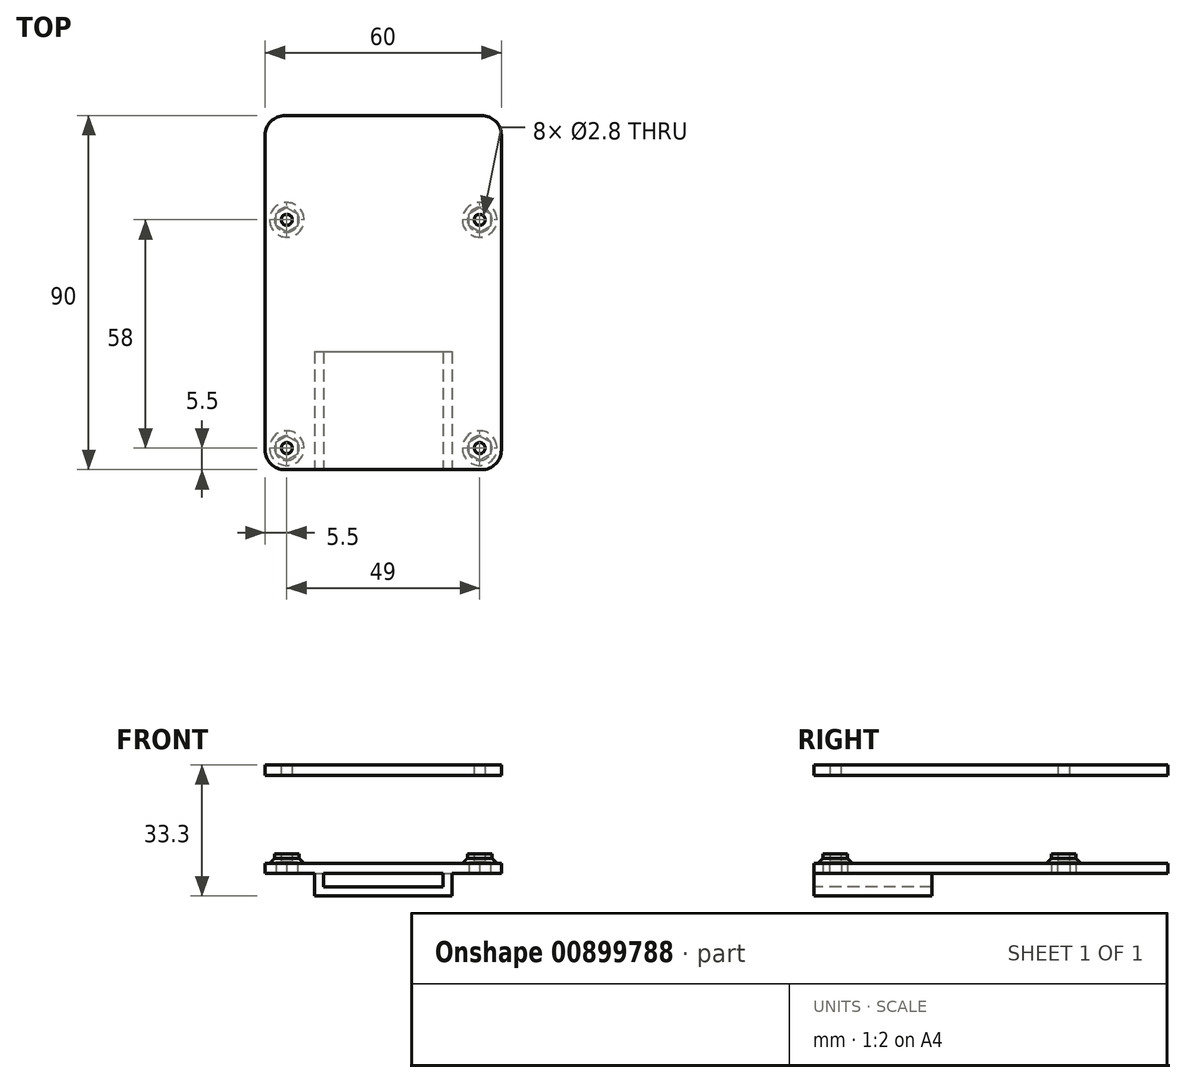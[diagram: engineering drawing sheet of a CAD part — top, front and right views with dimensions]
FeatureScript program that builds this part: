
annotation { "Feature Type Name" : "Feature", "Feature Type Description" : "" }
export const myFeature = defineFeature(function(context is Context, id is Id, definition is map)
    precondition{}
    {
        {
            var Q0;
            Q0=qCreatedBy(makeId("Top.planeOp"),FACE);
            var sketch = newSketch(context, id + "F0", { "sketchPlane" : qUnion([Q0])});
            skLineSegment(sketch, "E0.bottom", {"start": v(-30, 45) * mm, "end": v(30, 45) * mm});
            skLineSegment(sketch, "E0.top", {"start": v(-30, -45) * mm, "end": v(30, -45) * mm});
            skLineSegment(sketch, "E0.left", {"start": v(-30, 45) * mm, "end": v(-30, -45) * mm});
            skLineSegment(sketch, "E0.right", {"start": v(30, 45) * mm, "end": v(30, -45) * mm});
            skPoint(sketch, "E0.middle", {"position": v(0, 0) * mm});
            skLineSegment(sketch, "E1.bottom", {"start": v(-24.5, 18.5) * mm, "end": v(24.5, 18.5) * mm, "construction": true});
            skLineSegment(sketch, "E1.top", {"start": v(-24.5, -39.5) * mm, "end": v(24.5, -39.5) * mm, "construction": true});
            skLineSegment(sketch, "E1.left", {"start": v(-24.5, 18.5) * mm, "end": v(-24.5, -39.5) * mm, "construction": true});
            skLineSegment(sketch, "E1.right", {"start": v(24.5, 18.5) * mm, "end": v(24.5, -39.5) * mm, "construction": true});
            skPoint(sketch, "E1.middle", {"position": v(0, -10.5) * mm});
            skCircle(sketch, "E2", {"center": v(-24.5, 18.5) * mm, "radius": 1.4 * mm});
            skCircle(sketch, "E3", {"center": v(24.5, 18.5) * mm, "radius": 1.4 * mm});
            skCircle(sketch, "E4", {"center": v(-24.5, -39.5) * mm, "radius": 1.4 * mm});
            skCircle(sketch, "E5", {"center": v(24.5, -39.5) * mm, "radius": 1.4 * mm});
            skCircle(sketch, "E6", {"center": v(-24.5, 18.5) * mm, "radius": 3.12 * mm});
            skCircle(sketch, "E7", {"center": v(24.5, 18.5) * mm, "radius": 3.12 * mm});
            skCircle(sketch, "E8", {"center": v(-24.5, -39.5) * mm, "radius": 3.12 * mm});
            skCircle(sketch, "E9", {"center": v(24.5, -39.5) * mm, "radius": 3.12 * mm});
            skCircle(sketch, "E10.cCircle", {"center": v(-24.5, 18.5) * mm, "radius": 3.12 * mm, "construction": true});
            skLineSegment(sketch, "E10.0", {"start": v(-24.5, 21.62) * mm, "end": v(-21.8, 20.06) * mm});
            skLineSegment(sketch, "E10.1", {"start": v(-21.8, 20.06) * mm, "end": v(-21.8, 16.94) * mm});
            skLineSegment(sketch, "E10.2", {"start": v(-21.8, 16.94) * mm, "end": v(-24.5, 15.38) * mm});
            skLineSegment(sketch, "E10.3", {"start": v(-24.5, 15.38) * mm, "end": v(-27.2, 16.94) * mm});
            skLineSegment(sketch, "E10.4", {"start": v(-27.2, 16.94) * mm, "end": v(-27.2, 20.06) * mm});
            skLineSegment(sketch, "E10.5", {"start": v(-27.2, 20.06) * mm, "end": v(-24.5, 21.62) * mm});
            skCircle(sketch, "E11", {"center": v(-24.5, 18.5) * mm, "radius": 5 * mm});
            skCircle(sketch, "E12", {"center": v(24.5, 18.5) * mm, "radius": 5 * mm});
            skCircle(sketch, "E13", {"center": v(24.5, -39.5) * mm, "radius": 5 * mm});
            skCircle(sketch, "E14", {"center": v(-24.5, -39.5) * mm, "radius": 5 * mm});
            skCircle(sketch, "E15.cCircle", {"center": v(24.5, 18.5) * mm, "radius": 3.12 * mm, "construction": true});
            skLineSegment(sketch, "E15.0", {"start": v(24.5, 21.62) * mm, "end": v(27.2, 20.06) * mm});
            skLineSegment(sketch, "E15.1", {"start": v(27.2, 20.06) * mm, "end": v(27.2, 16.94) * mm});
            skLineSegment(sketch, "E15.2", {"start": v(27.2, 16.94) * mm, "end": v(24.5, 15.38) * mm});
            skLineSegment(sketch, "E15.3", {"start": v(24.5, 15.38) * mm, "end": v(21.8, 16.94) * mm});
            skLineSegment(sketch, "E15.4", {"start": v(21.8, 16.94) * mm, "end": v(21.8, 20.06) * mm});
            skLineSegment(sketch, "E15.5", {"start": v(21.8, 20.06) * mm, "end": v(24.5, 21.62) * mm});
            skCircle(sketch, "E16.cCircle", {"center": v(24.5, -39.5) * mm, "radius": 5 * mm, "construction": true});
            skCircle(sketch, "E17.cCircle", {"center": v(-24.5, -39.5) * mm, "radius": 3.12 * mm, "construction": true});
            skLineSegment(sketch, "E17.0", {"start": v(-24.5, -36.38) * mm, "end": v(-21.8, -37.94) * mm});
            skLineSegment(sketch, "E17.1", {"start": v(-21.8, -37.94) * mm, "end": v(-21.8, -41.06) * mm});
            skLineSegment(sketch, "E17.2", {"start": v(-21.8, -41.06) * mm, "end": v(-24.5, -42.62) * mm});
            skLineSegment(sketch, "E17.3", {"start": v(-24.5, -42.62) * mm, "end": v(-27.2, -41.06) * mm});
            skLineSegment(sketch, "E17.4", {"start": v(-27.2, -41.06) * mm, "end": v(-27.2, -37.94) * mm});
            skLineSegment(sketch, "E17.5", {"start": v(-27.2, -37.94) * mm, "end": v(-24.5, -36.38) * mm});
            skCircle(sketch, "E18.cCircle", {"center": v(24.5, -39.5) * mm, "radius": 3.12 * mm, "construction": true});
            skLineSegment(sketch, "E18.0", {"start": v(24.5, -36.38) * mm, "end": v(27.2, -37.94) * mm});
            skLineSegment(sketch, "E18.1", {"start": v(27.2, -37.94) * mm, "end": v(27.2, -41.06) * mm});
            skLineSegment(sketch, "E18.2", {"start": v(27.2, -41.06) * mm, "end": v(24.5, -42.62) * mm});
            skLineSegment(sketch, "E18.3", {"start": v(24.5, -42.62) * mm, "end": v(21.8, -41.06) * mm});
            skLineSegment(sketch, "E18.4", {"start": v(21.8, -41.06) * mm, "end": v(21.8, -37.94) * mm});
            skLineSegment(sketch, "E18.5", {"start": v(21.8, -37.94) * mm, "end": v(24.5, -36.38) * mm});
            skSolve(sketch);
        }
        {
            var Q0;
            Q0=makeQuery(id+"F0.imprint","IMPRINT",FACE,{"disambiguationData":[TD([[makeQuery(id+"F0.imprint","IMPRINT",EDGE,{"derivedFrom":sQuery(id+"F0.wireOp",EDGE,"E0.bottom")}),-1.0]])]});
            extrude(context, id + "F1", {"entities" : qUnion([Q0]), "depth" : 2.6 * mm, "offsetDistance" : 25 * mm});
        }
        {
            var Q0;
            Q0=makeQuery(id+"F1.opExtrude","SWEPT_EDGE",EDGE,{"disambiguationData":[OSD([sQuery(id+"F0.wireOp",EDGE,"E0.bottom"),sQuery(id+"F0.wireOp",EDGE,"E0.left")])]});
            var Q1;
            Q1=makeQuery(id+"F1.opExtrude","SWEPT_EDGE",EDGE,{"disambiguationData":[OSD([sQuery(id+"F0.wireOp",EDGE,"E0.bottom"),sQuery(id+"F0.wireOp",EDGE,"E0.right")])]});
            var Q2;
            Q2=makeQuery(id+"F1.opExtrude","SWEPT_EDGE",EDGE,{"disambiguationData":[OSD([sQuery(id+"F0.wireOp",EDGE,"E0.top"),sQuery(id+"F0.wireOp",EDGE,"E0.left")])]});
            var Q3;
            Q3=makeQuery(id+"F1.opExtrude","SWEPT_EDGE",EDGE,{"disambiguationData":[OSD([sQuery(id+"F0.wireOp",EDGE,"E0.top"),sQuery(id+"F0.wireOp",EDGE,"E0.right")])]});
            fillet(context, id + "F2", {"entities" : qUnion([Q0, Q1, Q2, Q3]), "radius" : 5 * mm, "tangentPropagation" : true, "allowEdgeOverflow" : false});
        }
        {
            var Q0;
            {var subQ0=sQuery(id+"F0.wireOp",EDGE,"E10.4");Q0=makeQuery(id+"F0.imprint","IMPRINT",FACE,{"disambiguationData":[TD([[makeQuery(id+"F0.imprint","IMPRINT",EDGE,{"derivedFrom":subQ0}),1.0]])]});}
            var Q1;
            Q1=makeQuery(id+"F0.imprint","IMPRINT",FACE,{"disambiguationData":[TD([[makeQuery(id+"F0.imprint","IMPRINT",EDGE,{"derivedFrom":sQuery(id+"F0.wireOp",EDGE,"E2")}),-1.0]])]});
            var Q2;
            {var subQ0=sQuery(id+"F0.wireOp",EDGE,"E10.5");Q2=makeQuery(id+"F0.imprint","IMPRINT",FACE,{"disambiguationData":[TD([[makeQuery(id+"F0.imprint","IMPRINT",EDGE,{"derivedFrom":subQ0}),1.0]])]});}
            var Q3;
            {var subQ0=sQuery(id+"F0.wireOp",EDGE,"E10.0");Q3=makeQuery(id+"F0.imprint","IMPRINT",FACE,{"disambiguationData":[TD([[makeQuery(id+"F0.imprint","IMPRINT",EDGE,{"derivedFrom":subQ0}),1.0]])]});}
            var Q4;
            {var subQ0=sQuery(id+"F0.wireOp",EDGE,"E10.1");Q4=makeQuery(id+"F0.imprint","IMPRINT",FACE,{"disambiguationData":[TD([[makeQuery(id+"F0.imprint","IMPRINT",EDGE,{"derivedFrom":subQ0}),1.0]])]});}
            var Q5;
            {var subQ0=sQuery(id+"F0.wireOp",EDGE,"E10.2");Q5=makeQuery(id+"F0.imprint","IMPRINT",FACE,{"disambiguationData":[TD([[makeQuery(id+"F0.imprint","IMPRINT",EDGE,{"derivedFrom":subQ0}),1.0]])]});}
            var Q6;
            {var subQ0=sQuery(id+"F0.wireOp",EDGE,"E10.3");Q6=makeQuery(id+"F0.imprint","IMPRINT",FACE,{"disambiguationData":[TD([[makeQuery(id+"F0.imprint","IMPRINT",EDGE,{"derivedFrom":subQ0}),1.0]])]});}
            var Q7;
            Q7=makeQuery(id+"F0.imprint","IMPRINT",FACE,{"disambiguationData":[TD([[makeQuery(id+"F0.imprint","IMPRINT",EDGE,{"derivedFrom":sQuery(id+"F0.wireOp",EDGE,"E3")}),-1.0]])]});
            var Q8;
            {var subQ0=sQuery(id+"F0.wireOp",EDGE,"E15.4");Q8=makeQuery(id+"F0.imprint","IMPRINT",FACE,{"disambiguationData":[TD([[makeQuery(id+"F0.imprint","IMPRINT",EDGE,{"derivedFrom":subQ0}),1.0]])]});}
            var Q9;
            {var subQ0=sQuery(id+"F0.wireOp",EDGE,"E15.5");Q9=makeQuery(id+"F0.imprint","IMPRINT",FACE,{"disambiguationData":[TD([[makeQuery(id+"F0.imprint","IMPRINT",EDGE,{"derivedFrom":subQ0}),1.0]])]});}
            var Q10;
            {var subQ0=sQuery(id+"F0.wireOp",EDGE,"E15.0");Q10=makeQuery(id+"F0.imprint","IMPRINT",FACE,{"disambiguationData":[TD([[makeQuery(id+"F0.imprint","IMPRINT",EDGE,{"derivedFrom":subQ0}),1.0]])]});}
            var Q11;
            {var subQ0=sQuery(id+"F0.wireOp",EDGE,"E15.1");Q11=makeQuery(id+"F0.imprint","IMPRINT",FACE,{"disambiguationData":[TD([[makeQuery(id+"F0.imprint","IMPRINT",EDGE,{"derivedFrom":subQ0}),1.0]])]});}
            var Q12;
            {var subQ0=sQuery(id+"F0.wireOp",EDGE,"E15.2");Q12=makeQuery(id+"F0.imprint","IMPRINT",FACE,{"disambiguationData":[TD([[makeQuery(id+"F0.imprint","IMPRINT",EDGE,{"derivedFrom":subQ0}),1.0]])]});}
            var Q13;
            {var subQ0=sQuery(id+"F0.wireOp",EDGE,"E15.3");Q13=makeQuery(id+"F0.imprint","IMPRINT",FACE,{"disambiguationData":[TD([[makeQuery(id+"F0.imprint","IMPRINT",EDGE,{"derivedFrom":subQ0}),1.0]])]});}
            var Q14;
            {var subQ0=sQuery(id+"F0.wireOp",EDGE,"E18.5");Q14=makeQuery(id+"F0.imprint","IMPRINT",FACE,{"disambiguationData":[TD([[makeQuery(id+"F0.imprint","IMPRINT",EDGE,{"derivedFrom":subQ0}),1.0]])]});}
            var Q15;
            Q15=makeQuery(id+"F0.imprint","IMPRINT",FACE,{"disambiguationData":[TD([[makeQuery(id+"F0.imprint","IMPRINT",EDGE,{"derivedFrom":sQuery(id+"F0.wireOp",EDGE,"E5")}),-1.0]])]});
            var Q16;
            {var subQ0=sQuery(id+"F0.wireOp",EDGE,"E18.0");Q16=makeQuery(id+"F0.imprint","IMPRINT",FACE,{"disambiguationData":[TD([[makeQuery(id+"F0.imprint","IMPRINT",EDGE,{"derivedFrom":subQ0}),1.0]])]});}
            var Q17;
            {var subQ0=sQuery(id+"F0.wireOp",EDGE,"E18.1");Q17=makeQuery(id+"F0.imprint","IMPRINT",FACE,{"disambiguationData":[TD([[makeQuery(id+"F0.imprint","IMPRINT",EDGE,{"derivedFrom":subQ0}),1.0]])]});}
            var Q18;
            {var subQ0=sQuery(id+"F0.wireOp",EDGE,"E18.2");Q18=makeQuery(id+"F0.imprint","IMPRINT",FACE,{"disambiguationData":[TD([[makeQuery(id+"F0.imprint","IMPRINT",EDGE,{"derivedFrom":subQ0}),1.0]])]});}
            var Q19;
            {var subQ0=sQuery(id+"F0.wireOp",EDGE,"E18.3");Q19=makeQuery(id+"F0.imprint","IMPRINT",FACE,{"disambiguationData":[TD([[makeQuery(id+"F0.imprint","IMPRINT",EDGE,{"derivedFrom":subQ0}),1.0]])]});}
            var Q20;
            {var subQ0=sQuery(id+"F0.wireOp",EDGE,"E18.4");Q20=makeQuery(id+"F0.imprint","IMPRINT",FACE,{"disambiguationData":[TD([[makeQuery(id+"F0.imprint","IMPRINT",EDGE,{"derivedFrom":subQ0}),1.0]])]});}
            var Q21;
            Q21=makeQuery(id+"F0.imprint","IMPRINT",FACE,{"disambiguationData":[TD([[makeQuery(id+"F0.imprint","IMPRINT",EDGE,{"derivedFrom":sQuery(id+"F0.wireOp",EDGE,"E4")}),-1.0]])]});
            var Q22;
            {var subQ0=sQuery(id+"F0.wireOp",EDGE,"E17.5");Q22=makeQuery(id+"F0.imprint","IMPRINT",FACE,{"disambiguationData":[TD([[makeQuery(id+"F0.imprint","IMPRINT",EDGE,{"derivedFrom":subQ0}),1.0]])]});}
            var Q23;
            {var subQ0=sQuery(id+"F0.wireOp",EDGE,"E17.0");Q23=makeQuery(id+"F0.imprint","IMPRINT",FACE,{"disambiguationData":[TD([[makeQuery(id+"F0.imprint","IMPRINT",EDGE,{"derivedFrom":subQ0}),1.0]])]});}
            var Q24;
            {var subQ0=sQuery(id+"F0.wireOp",EDGE,"E17.1");Q24=makeQuery(id+"F0.imprint","IMPRINT",FACE,{"disambiguationData":[TD([[makeQuery(id+"F0.imprint","IMPRINT",EDGE,{"derivedFrom":subQ0}),1.0]])]});}
            var Q25;
            {var subQ0=sQuery(id+"F0.wireOp",EDGE,"E17.2");Q25=makeQuery(id+"F0.imprint","IMPRINT",FACE,{"disambiguationData":[TD([[makeQuery(id+"F0.imprint","IMPRINT",EDGE,{"derivedFrom":subQ0}),1.0]])]});}
            var Q26;
            {var subQ0=sQuery(id+"F0.wireOp",EDGE,"E17.3");Q26=makeQuery(id+"F0.imprint","IMPRINT",FACE,{"disambiguationData":[TD([[makeQuery(id+"F0.imprint","IMPRINT",EDGE,{"derivedFrom":subQ0}),1.0]])]});}
            var Q27;
            {var subQ0=sQuery(id+"F0.wireOp",EDGE,"E17.4");Q27=makeQuery(id+"F0.imprint","IMPRINT",FACE,{"disambiguationData":[TD([[makeQuery(id+"F0.imprint","IMPRINT",EDGE,{"derivedFrom":subQ0}),1.0]])]});}
            extrude(context, id + "F3", {"entities" : qUnion([Q0, Q1, Q2, Q3, Q4, Q5, Q6, Q7, Q8, Q9, Q10, Q11, Q12, Q13, Q14, Q15, Q16, Q17, Q18, Q19, Q20, Q21, Q22, Q23, Q24, Q25, Q26, Q27]), "operationType" : NewBodyOperationType.ADD, "surfaceOperationType" : NewSurfaceOperationType.ADD, "depth" : 5 * mm, "offsetDistance" : 25 * mm});
        }
        {
            var Q0;
            Q0=makeQuery(id+"F0.imprint","IMPRINT",FACE,{"disambiguationData":[TD([[makeQuery(id+"F0.imprint","IMPRINT",EDGE,{"derivedFrom":sQuery(id+"F0.wireOp",EDGE,"E11")}),1.0]])]});
            var Q1;
            Q1=makeQuery(id+"F0.imprint","IMPRINT",FACE,{"disambiguationData":[TD([[makeQuery(id+"F0.imprint","IMPRINT",EDGE,{"derivedFrom":sQuery(id+"F0.wireOp",EDGE,"E12")}),1.0]])]});
            var Q2;
            Q2=makeQuery(id+"F0.imprint","IMPRINT",FACE,{"disambiguationData":[TD([[makeQuery(id+"F0.imprint","IMPRINT",EDGE,{"derivedFrom":sQuery(id+"F0.wireOp",EDGE,"E13")}),1.0]])]});
            var Q3;
            Q3=makeQuery(id+"F0.imprint","IMPRINT",FACE,{"disambiguationData":[TD([[makeQuery(id+"F0.imprint","IMPRINT",EDGE,{"derivedFrom":sQuery(id+"F0.wireOp",EDGE,"E14")}),1.0]])]});
            extrude(context, id + "F4", {"entities" : qUnion([Q0, Q1, Q2, Q3]), "operationType" : NewBodyOperationType.ADD, "depth" : 4 * mm, "offsetDistance" : 25 * mm});
        }
        {
            var Q0;
            Q0=makeQuery(id+"F4.opExtrude","CAP_EDGE",EDGE,{"disambiguationData":[OSD([sQuery(id+"F0.wireOp",EDGE,"E11")])],"isStart":false});
            var Q1;
            Q1=makeQuery(id+"F4.opExtrude","CAP_EDGE",EDGE,{"disambiguationData":[OSD([sQuery(id+"F0.wireOp",EDGE,"E14")])],"isStart":false});
            var Q2;
            Q2=makeQuery(id+"F4.opExtrude","CAP_EDGE",EDGE,{"disambiguationData":[OSD([sQuery(id+"F0.wireOp",EDGE,"E13")])],"isStart":false});
            var Q3;
            Q3=makeQuery(id+"F4.opExtrude","CAP_EDGE",EDGE,{"disambiguationData":[OSD([sQuery(id+"F0.wireOp",EDGE,"E12")])],"isStart":false});
            chamfer(context, id + "F5", {"entities" : qUnion([Q0, Q1, Q2, Q3]), "width" : 2 * mm, "tangentPropagation" : true});
        }
        {
            var Q0;
            Q0=makeQuery(id+"F0.imprint","IMPRINT",FACE,{"disambiguationData":[TD([[makeQuery(id+"F0.imprint","IMPRINT",EDGE,{"derivedFrom":sQuery(id+"F0.wireOp",EDGE,"E2")}),-1.0]])]});
            var Q1;
            Q1=makeQuery(id+"F0.imprint","IMPRINT",FACE,{"disambiguationData":[TD([[makeQuery(id+"F0.imprint","IMPRINT",EDGE,{"derivedFrom":sQuery(id+"F0.wireOp",EDGE,"E3")}),-1.0]])]});
            var Q2;
            Q2=makeQuery(id+"F0.imprint","IMPRINT",FACE,{"disambiguationData":[TD([[makeQuery(id+"F0.imprint","IMPRINT",EDGE,{"derivedFrom":sQuery(id+"F0.wireOp",EDGE,"E5")}),-1.0]])]});
            var Q3;
            Q3=makeQuery(id+"F0.imprint","IMPRINT",FACE,{"disambiguationData":[TD([[makeQuery(id+"F0.imprint","IMPRINT",EDGE,{"derivedFrom":sQuery(id+"F0.wireOp",EDGE,"E4")}),-1.0]])]});
            extrude(context, id + "F6", {"entities" : qUnion([Q0, Q1, Q2, Q3]), "operationType" : NewBodyOperationType.REMOVE, "depth" : 3 * mm, "offsetDistance" : 25 * mm});
        }
        {
            var Q0;
            Q0=makeQuery(id+"F1.opExtrude","SWEPT_FACE",FACE,{"disambiguationData":[OSD([sQuery(id+"F0.wireOp",EDGE,"E0.top")])]});
            var sketch = newSketch(context, id + "F7", { "sketchPlane" : qUnion([Q0])});
            skPoint(sketch, "E19.0", {"position": v(0, 0) * mm});
            skLineSegment(sketch, "E20.bottom", {"start": v(-15.2, 0) * mm, "end": v(15.2, 0) * mm});
            skLineSegment(sketch, "E20.top", {"start": v(-15.2, -3.4) * mm, "end": v(15.2, -3.4) * mm});
            skLineSegment(sketch, "E20.left", {"start": v(-15.2, 0) * mm, "end": v(-15.2, -3.4) * mm});
            skLineSegment(sketch, "E20.right", {"start": v(15.2, 0) * mm, "end": v(15.2, -3.4) * mm});
            skPoint(sketch, "E20.middle", {"position": v(0, -1.7) * mm});
            skLineSegment(sketch, "E21.bottom", {"start": v(-17.5, 2.3) * mm, "end": v(17.5, 2.3) * mm});
            skLineSegment(sketch, "E21.top", {"start": v(-17.5, -5.7) * mm, "end": v(17.5, -5.7) * mm});
            skLineSegment(sketch, "E21.left", {"start": v(-17.5, 2.3) * mm, "end": v(-17.5, -5.7) * mm});
            skLineSegment(sketch, "E21.right", {"start": v(17.5, 2.3) * mm, "end": v(17.5, -5.7) * mm});
            skSolve(sketch);
        }
        {
            var Q0;
            Q0=makeQuery(id+"F7.imprint","IMPRINT",FACE,{"disambiguationData":[TD([[makeQuery(id+"F7.imprint","IMPRINT",EDGE,{"derivedFrom":sQuery(id+"F7.wireOp",EDGE,"E20.bottom")}),1.0]])]});
            var Q1;
            Q1=makeQuery(id+"F7.imprint","IMPRINT",FACE,{"disambiguationData":[TD([[makeQuery(id+"F7.imprint","IMPRINT",EDGE,{"derivedFrom":sQuery(id+"F7.wireOp",EDGE,"E20.top")}),-1.0]])]});
            extrude(context, id + "F8", {"entities" : qUnion([Q0, Q1]), "operationType" : NewBodyOperationType.ADD, "oppositeDirection" : true, "depth" : 30 * mm, "offsetDistance" : 25 * mm});
        }
        {
            var Q0;
            Q0=qCreatedBy(makeId("Top.planeOp"),FACE);
            cPlane(context, id + "F9", {"entities" : qUnion([Q0]), "cplaneType" : CPlaneType.OFFSET, "offset" : 25 * mm, "width" : 150 * mm, "height" : 150 * mm});
        }
        {
            var Q0;
            Q0=qCreatedBy(id+"F9.planeOp",FACE);
            var sketch = newSketch(context, id + "F10", { "sketchPlane" : qUnion([Q0])});
            skCircle(sketch, "E22.0", {"center": v(-24.5, 18.5) * mm, "radius": 1.4 * mm});
            skCircle(sketch, "E22.1", {"center": v(24.5, 18.5) * mm, "radius": 1.4 * mm});
            skCircle(sketch, "E22.2", {"center": v(-24.5, -39.5) * mm, "radius": 1.4 * mm});
            skCircle(sketch, "E22.3", {"center": v(24.5, -39.5) * mm, "radius": 1.4 * mm});
            skLineSegment(sketch, "E22.4", {"start": v(30, 45) * mm, "end": v(30, -45) * mm});
            skLineSegment(sketch, "E22.5", {"start": v(-17.5, -45) * mm, "end": v(17.5, -45) * mm});
            skLineSegment(sketch, "E22.6", {"start": v(-30, 45) * mm, "end": v(30, 45) * mm});
            skLineSegment(sketch, "E22.7", {"start": v(-30, 45) * mm, "end": v(-30, -45) * mm});
            skLineSegment(sketch, "E22.8", {"start": v(-30, -45) * mm, "end": v(30, -45) * mm});
            skPoint(sketch, "E22.9", {"position": v(-30, 0) * mm});
            skSolve(sketch);
        }
        {
            var Q0;
            Q0 = qSketchRegion(id + "F10", true);
            extrude(context, id + "F11", {"entities" : qUnion([Q0]), "depth" : 2.6 * mm, "offsetDistance" : 25 * mm});
        }
        {
            var Q0;
            Q0=makeQuery(id+"F11.opExtrude","SWEPT_EDGE",EDGE,{"disambiguationData":[OSD([sQuery(id+"F10.wireOp",EDGE,"E22.6"),sQuery(id+"F10.wireOp",EDGE,"E22.7")])]});
            var Q1;
            Q1=makeQuery(id+"F11.opExtrude","SWEPT_EDGE",EDGE,{"disambiguationData":[OSD([sQuery(id+"F10.wireOp",EDGE,"E22.4"),sQuery(id+"F10.wireOp",EDGE,"E22.6")])]});
            var Q2;
            Q2=makeQuery(id+"F11.opExtrude","SWEPT_EDGE",EDGE,{"disambiguationData":[OSD([sQuery(id+"F10.wireOp",EDGE,"E22.4"),sQuery(id+"F10.wireOp",EDGE,"E22.8")])]});
            var Q3;
            Q3=makeQuery(id+"F11.opExtrude","SWEPT_EDGE",EDGE,{"disambiguationData":[OSD([sQuery(id+"F10.wireOp",EDGE,"E22.7"),sQuery(id+"F10.wireOp",EDGE,"E22.8")])]});
            fillet(context, id + "F12", {"entities" : qUnion([Q0, Q1, Q2, Q3]), "radius" : 5 * mm, "tangentPropagation" : true, "allowEdgeOverflow" : false});
        }
    });
